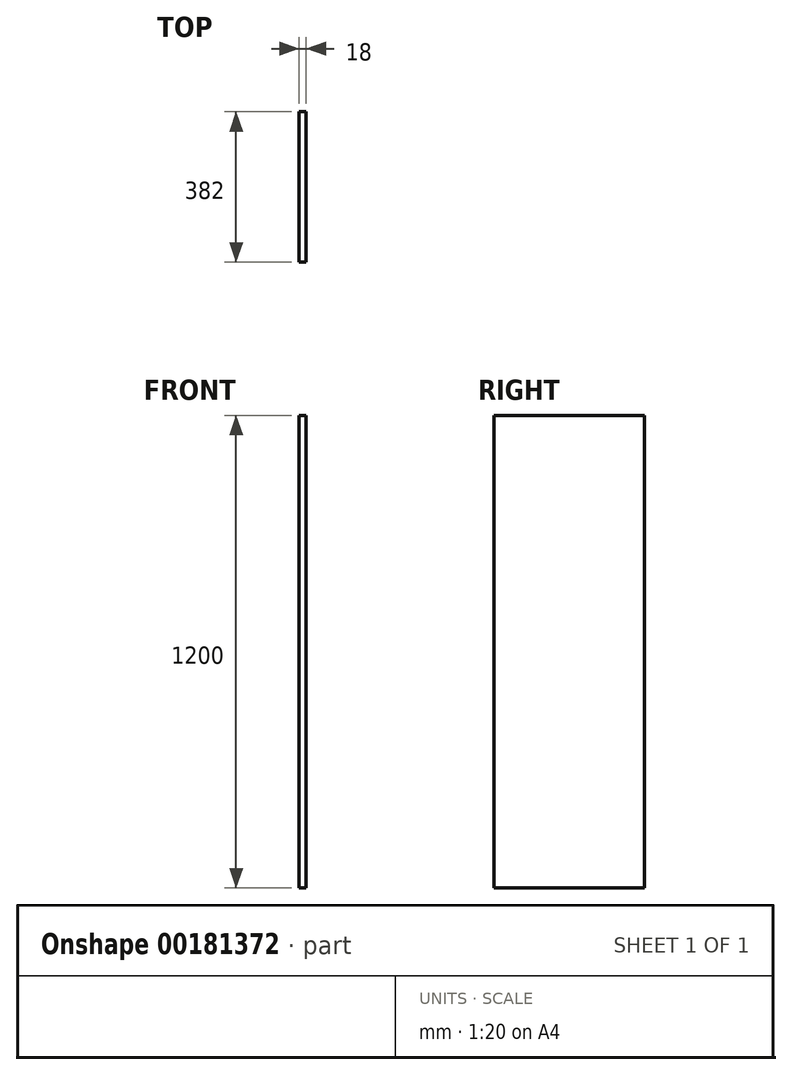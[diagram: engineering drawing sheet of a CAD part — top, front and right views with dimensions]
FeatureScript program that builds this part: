
annotation { "Feature Type Name" : "Feature", "Feature Type Description" : "" }
export const myFeature = defineFeature(function(context is Context, id is Id, definition is map)
    precondition{}
    {
        {
            var Q0;
            Q0=qCreatedBy(makeId("Right.planeOp"),FACE);
            var sketch = newSketch(context, id + "F0", { "sketchPlane" : qUnion([Q0])});
            skLineSegment(sketch, "E0.bottom", {"start": v(-191, 600) * mm, "end": v(191, 600) * mm});
            skLineSegment(sketch, "E0.top", {"start": v(-191, -600) * mm, "end": v(191, -600) * mm});
            skLineSegment(sketch, "E0.left", {"start": v(-191, 600) * mm, "end": v(-191, -600) * mm});
            skLineSegment(sketch, "E0.right", {"start": v(191, 600) * mm, "end": v(191, -600) * mm});
            skPoint(sketch, "E0.middle", {"position": v(0, 0) * mm});
            skSolve(sketch);
        }
        {
            var Q0;
            Q0 = qSketchRegion(id + "F0", true);
            extrude(context, id + "F1", {"entities" : qUnion([Q0]), "depth" : 18 * mm});
        }
    });
